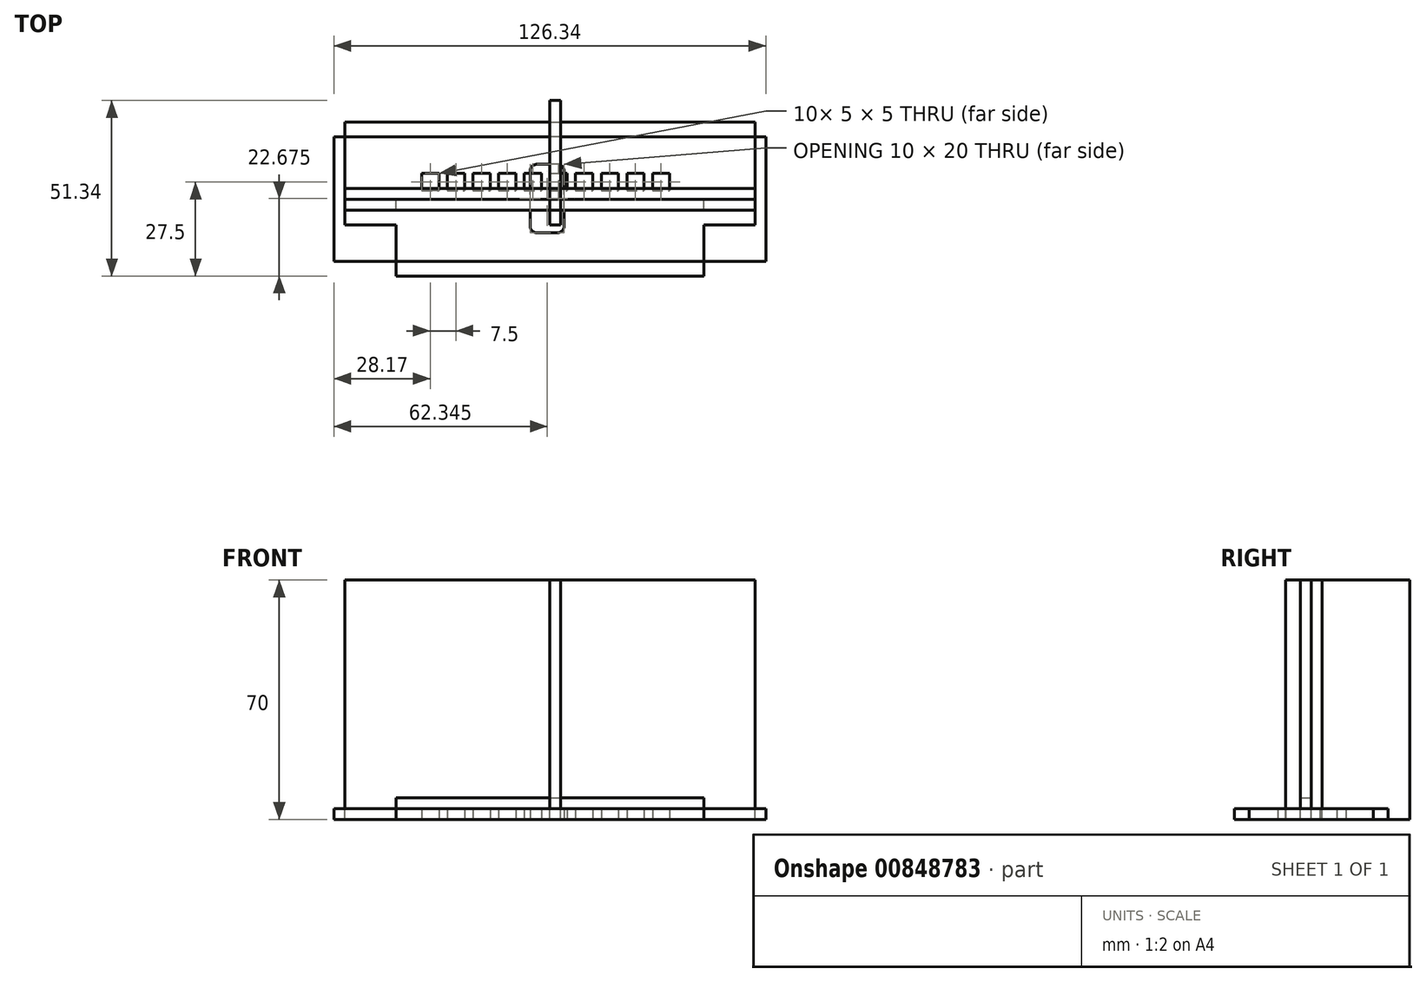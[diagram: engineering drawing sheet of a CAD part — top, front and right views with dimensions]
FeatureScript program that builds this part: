
annotation { "Feature Type Name" : "Feature", "Feature Type Description" : "" }
export const myFeature = defineFeature(function(context is Context, id is Id, definition is map)
    precondition{}
    {
        {
            var Q0;
            Q0=qCreatedBy(makeId("Top.planeOp"),FACE);
            var sketch = newSketch(context, id + "F0", { "sketchPlane" : qUnion([Q0])});
            skLineSegment(sketch, "E0.bottom", {"start": v(45, -22.5) * mm, "end": v(-45, -22.5) * mm});
            skLineSegment(sketch, "E0.top", {"start": v(45, 22.5) * mm, "end": v(-45, 22.5) * mm});
            skLineSegment(sketch, "E0.left", {"start": v(45, -22.5) * mm, "end": v(45, 22.5) * mm});
            skLineSegment(sketch, "E0.right", {"start": v(-45, -22.5) * mm, "end": v(-45, 22.5) * mm});
            skPoint(sketch, "E0.middle", {"position": v(0, 0) * mm});
            skLineSegment(sketch, "E1.bottom", {"start": v(-45, 22.5) * mm, "end": v(-60, 22.5) * mm});
            skLineSegment(sketch, "E1.left", {"start": v(-45, 22.5) * mm, "end": v(-45, -22.5) * mm});
            skLineSegment(sketch, "E2.bottom", {"start": v(-60, -7.5) * mm, "end": v(-45, -7.5) * mm});
            skLineSegment(sketch, "E2.right", {"start": v(-45, -7.5) * mm, "end": v(-45, -10.68) * mm});
            skLineSegment(sketch, "E3.MirrorCS", {"start": v(45, 22.5) * mm, "end": v(60, 22.5) * mm});
            skLineSegment(sketch, "E4.MirrorCS", {"start": v(60, -7.5) * mm, "end": v(45, -7.5) * mm});
            skLineSegment(sketch, "E5.bottom", {"start": v(-37.5, 7.5) * mm, "end": v(-32.5, 7.5) * mm});
            skLineSegment(sketch, "E5.top", {"start": v(-37.5, 2.5) * mm, "end": v(-32.5, 2.5) * mm});
            skLineSegment(sketch, "E5.left", {"start": v(-37.5, 7.5) * mm, "end": v(-37.5, 2.5) * mm});
            skLineSegment(sketch, "E5.right", {"start": v(-32.5, 7.5) * mm, "end": v(-32.5, 2.5) * mm});
            skLineSegment(sketch, "E6.1.0.0", {"start": v(-30, 7.5) * mm, "end": v(-25, 7.5) * mm});
            skLineSegment(sketch, "E6.1.0.1", {"start": v(-30, 7.5) * mm, "end": v(-30, 2.5) * mm});
            skLineSegment(sketch, "E6.1.0.2", {"start": v(-30, 2.5) * mm, "end": v(-25, 2.5) * mm});
            skLineSegment(sketch, "E6.1.0.3", {"start": v(-25, 7.5) * mm, "end": v(-25, 2.5) * mm});
            skLineSegment(sketch, "E6.2.0.0", {"start": v(-22.5, 7.5) * mm, "end": v(-17.5, 7.5) * mm});
            skLineSegment(sketch, "E6.2.0.1", {"start": v(-22.5, 7.5) * mm, "end": v(-22.5, 2.5) * mm});
            skLineSegment(sketch, "E6.2.0.2", {"start": v(-22.5, 2.5) * mm, "end": v(-17.5, 2.5) * mm});
            skLineSegment(sketch, "E6.2.0.3", {"start": v(-17.5, 7.5) * mm, "end": v(-17.5, 2.5) * mm});
            skLineSegment(sketch, "E6.3.0.0", {"start": v(-15, 7.5) * mm, "end": v(-10, 7.5) * mm});
            skLineSegment(sketch, "E6.3.0.1", {"start": v(-15, 7.5) * mm, "end": v(-15, 2.5) * mm});
            skLineSegment(sketch, "E6.3.0.2", {"start": v(-15, 2.5) * mm, "end": v(-10, 2.5) * mm});
            skLineSegment(sketch, "E6.3.0.3", {"start": v(-10, 7.5) * mm, "end": v(-10, 2.5) * mm});
            skLineSegment(sketch, "E6.4.0.0", {"start": v(-7.5, 7.5) * mm, "end": v(-2.5, 7.5) * mm});
            skLineSegment(sketch, "E6.4.0.1", {"start": v(-7.5, 7.5) * mm, "end": v(-7.5, 2.5) * mm});
            skLineSegment(sketch, "E6.4.0.2", {"start": v(-7.5, 2.5) * mm, "end": v(-2.5, 2.5) * mm});
            skLineSegment(sketch, "E6.4.0.3", {"start": v(-2.5, 7.5) * mm, "end": v(-2.5, 2.5) * mm});
            skLineSegment(sketch, "E6.5.0.0", {"start": v(0, 7.5) * mm, "end": v(5, 7.5) * mm});
            skLineSegment(sketch, "E6.5.0.1", {"start": v(0, 7.5) * mm, "end": v(0, 2.5) * mm});
            skLineSegment(sketch, "E6.5.0.2", {"start": v(0, 2.5) * mm, "end": v(5, 2.5) * mm});
            skLineSegment(sketch, "E6.5.0.3", {"start": v(5, 7.5) * mm, "end": v(5, 2.5) * mm});
            skLineSegment(sketch, "E6.6.0.0", {"start": v(7.5, 7.5) * mm, "end": v(12.5, 7.5) * mm});
            skLineSegment(sketch, "E6.6.0.1", {"start": v(7.5, 7.5) * mm, "end": v(7.5, 2.5) * mm});
            skLineSegment(sketch, "E6.6.0.2", {"start": v(7.5, 2.5) * mm, "end": v(12.5, 2.5) * mm});
            skLineSegment(sketch, "E6.6.0.3", {"start": v(12.5, 7.5) * mm, "end": v(12.5, 2.5) * mm});
            skLineSegment(sketch, "E6.7.0.0", {"start": v(15, 7.5) * mm, "end": v(20, 7.5) * mm});
            skLineSegment(sketch, "E6.7.0.1", {"start": v(15, 7.5) * mm, "end": v(15, 2.5) * mm});
            skLineSegment(sketch, "E6.7.0.2", {"start": v(15, 2.5) * mm, "end": v(20, 2.5) * mm});
            skLineSegment(sketch, "E6.7.0.3", {"start": v(20, 7.5) * mm, "end": v(20, 2.5) * mm});
            skLineSegment(sketch, "E6.8.0.0", {"start": v(22.5, 7.5) * mm, "end": v(27.5, 7.5) * mm});
            skLineSegment(sketch, "E6.8.0.1", {"start": v(22.5, 7.5) * mm, "end": v(22.5, 2.5) * mm});
            skLineSegment(sketch, "E6.8.0.2", {"start": v(22.5, 2.5) * mm, "end": v(27.5, 2.5) * mm});
            skLineSegment(sketch, "E6.8.0.3", {"start": v(27.5, 7.5) * mm, "end": v(27.5, 2.5) * mm});
            skLineSegment(sketch, "E6.9.0.0", {"start": v(30, 7.5) * mm, "end": v(35, 7.5) * mm});
            skLineSegment(sketch, "E6.9.0.1", {"start": v(30, 7.5) * mm, "end": v(30, 2.5) * mm});
            skLineSegment(sketch, "E6.9.0.2", {"start": v(30, 2.5) * mm, "end": v(35, 2.5) * mm});
            skLineSegment(sketch, "E6.9.0.3", {"start": v(35, 7.5) * mm, "end": v(35, 2.5) * mm});
            skLineSegment(sketch, "E6.direction1", {"start": v(-37.5, 7.5) * mm, "end": v(-30, 7.5) * mm, "construction": true});
            skPoint(sketch, "E7.middle", {"position": v(0, 18.18) * mm});
            skLineSegment(sketch, "E8", {"start": v(-60, -7.5) * mm, "end": v(-60, 22.5) * mm});
            skLineSegment(sketch, "E9", {"start": v(60, 22.5) * mm, "end": v(60, -7.5) * mm});
            skSolve(sketch);
        }
        {
            var Q0;
            {var subQ0=sQuery(id+"F0.wireOp",EDGE,"1d0d9cd3-5991-4caf-813b-380c669309750.MirrorCS");Q0=makeQuery(id+"F0.imprint","IMPRINT",FACE,{"disambiguationData":[TD([[makeQuery(id+"F0.imprint","IMPRINT",EDGE,{"derivedFrom":subQ0}),1.0]])]});}
            var Q1;
            {var subQ0=sQuery(id+"F0.wireOp",EDGE,"E3.MirrorCS");Q1=makeQuery(id+"F0.imprint","IMPRINT",FACE,{"disambiguationData":[TD([[makeQuery(id+"F0.imprint","IMPRINT",EDGE,{"derivedFrom":subQ0}),-1.0]])]});}
            var Q2;
            {var subQ0=sQuery(id+"F0.wireOp",EDGE,"E1.bottom");Q2=makeQuery(id+"F0.imprint","IMPRINT",FACE,{"disambiguationData":[TD([[makeQuery(id+"F0.imprint","IMPRINT",EDGE,{"derivedFrom":subQ0}),1.0]])]});}
            var Q3;
            {var subQ0=sQuery(id+"F0.wireOp",EDGE,"E1.top");Q3=makeQuery(id+"F0.imprint","IMPRINT",FACE,{"disambiguationData":[TD([[makeQuery(id+"F0.imprint","IMPRINT",EDGE,{"derivedFrom":subQ0}),-1.0]])]});}
            var Q4;
            {var subQ4=sQuery(id+"F0.wireOp",EDGE,"E0.bottom");Q4=makeQuery(id+"F0.imprint","IMPRINT",FACE,{"disambiguationData":[TD([[makeQuery(id+"F0.imprint","IMPRINT",EDGE,{"derivedFrom":subQ4}),-1.0]])]});}
            var Q5;
            Q5=makeQuery(id+"F0.imprint","IMPRINT",FACE,{"disambiguationData":[TD([[makeQuery(id+"F0.imprint","IMPRINT",EDGE,{"derivedFrom":sQuery(id+"F0.wireOp",EDGE,"E5.bottom")}),1.0]])]});
            var Q6;
            {var subQ5=sQuery(id+"F0.wireOp",EDGE,"E7.bottom");Q6=makeQuery(id+"F0.imprint","IMPRINT",FACE,{"disambiguationData":[TD([[makeQuery(id+"F0.imprint","IMPRINT",EDGE,{"derivedFrom":subQ5}),-1.0]])]});}
            var Q7;
            {var subQ0=sQuery(id+"F0.wireOp",EDGE,"E2.bottom");Q7=makeQuery(id+"F0.imprint","IMPRINT",FACE,{"disambiguationData":[TD([[makeQuery(id+"F0.imprint","IMPRINT",EDGE,{"derivedFrom":subQ0}),1.0]])]});}
            var Q8;
            {var subQ0=sQuery(id+"F0.wireOp",EDGE,"E4.MirrorCS");Q8=makeQuery(id+"F0.imprint","IMPRINT",FACE,{"disambiguationData":[TD([[makeQuery(id+"F0.imprint","IMPRINT",EDGE,{"derivedFrom":subQ0}),-1.0]])]});}
            extrude(context, id + "F1", {"entities" : qUnion([Q0, Q1, Q2, Q3, Q4, Q5, Q6, Q7, Q8]), "depth" : 3.17 * mm, "offsetDistance" : 25 * mm});
        }
        {
            var Q0;
            Q0=qCreatedBy(makeId("Front.planeOp"),FACE);
            var sketch = newSketch(context, id + "F2", { "sketchPlane" : qUnion([Q0])});
            skLineSegment(sketch, "E10.bottom", {"start": v(-60, 0) * mm, "end": v(60, 0) * mm});
            skLineSegment(sketch, "E10.top", {"start": v(-60, 70) * mm, "end": v(60, 70) * mm});
            skLineSegment(sketch, "E10.left", {"start": v(-60, 0) * mm, "end": v(-60, 70) * mm});
            skLineSegment(sketch, "E10.right", {"start": v(60, 0) * mm, "end": v(60, 70) * mm});
            skLineSegment(sketch, "E11.bottom", {"start": v(-45, 0) * mm, "end": v(45, 0) * mm});
            skLineSegment(sketch, "E11.top", {"start": v(-45, 6.35) * mm, "end": v(45, 6.35) * mm});
            skLineSegment(sketch, "E11.left", {"start": v(-45, 0) * mm, "end": v(-45, 6.35) * mm});
            skLineSegment(sketch, "E11.right", {"start": v(45, 0) * mm, "end": v(45, 6.35) * mm});
            skSolve(sketch);
        }
        {
            var Q0;
            Q0=makeQuery(id+"F2.imprint","IMPRINT",FACE,{"disambiguationData":[TD([[makeQuery(id+"F2.imprint","IMPRINT",EDGE,{"derivedFrom":sQuery(id+"F2.wireOp",EDGE,"E10.top")}),-1.0]])]});
            extrude(context, id + "F3", {"entities" : qUnion([Q0]), "depth" : 3.17 * mm, "offsetDistance" : 25 * mm});
        }
        {
            var Q0;
            Q0 = qSketchRegion(id + "F2", true);
            extrude(context, id + "F4", {"entities" : qUnion([Q0]), "oppositeDirection" : true, "depth" : 3.17 * mm, "offsetDistance" : 25 * mm});
        }
        {
            var Q0;
            Q0=qCreatedBy(makeId("Right.planeOp"),FACE);
            var sketch = newSketch(context, id + "F5", { "sketchPlane" : qUnion([Q0])});
            skLineSegment(sketch, "E12.bottom", {"start": v(-7.51, 0) * mm, "end": v(28.84, 0) * mm});
            skLineSegment(sketch, "E12.top", {"start": v(-7.51, 70) * mm, "end": v(28.84, 70) * mm});
            skLineSegment(sketch, "E12.left", {"start": v(-7.51, 0) * mm, "end": v(-7.51, 70) * mm});
            skLineSegment(sketch, "E12.right", {"start": v(28.84, 0) * mm, "end": v(28.84, 70) * mm});
            skSolve(sketch);
        }
        {
            var Q0;
            Q0=makeQuery(id+"F5.imprint","IMPRINT",FACE,{"disambiguationData":[TD([[makeQuery(id+"F5.imprint","IMPRINT",EDGE,{"derivedFrom":sQuery(id+"F5.wireOp",EDGE,"E12.bottom")}),1.0]])]});
            extrude(context, id + "F6", {"entities" : qUnion([Q0]), "depth" : 3.17 * mm, "offsetDistance" : 25 * mm});
        }
        {
            var Q0;
            Q0=qCreatedBy(makeId("Top.planeOp"),FACE);
            var sketch = newSketch(context, id + "F7", { "sketchPlane" : qUnion([Q0])});
            skLineSegment(sketch, "E13.bottom", {"start": v(63.17, -18.17) * mm, "end": v(-63.17, -18.18) * mm});
            skLineSegment(sketch, "E13.top", {"start": v(63.17, 18.18) * mm, "end": v(-63.17, 18.17) * mm});
            skLineSegment(sketch, "E13.left", {"start": v(63.17, -18.17) * mm, "end": v(63.17, 18.18) * mm});
            skLineSegment(sketch, "E13.right", {"start": v(-63.17, -18.18) * mm, "end": v(-63.17, 18.17) * mm});
            skPoint(sketch, "E13.middle", {"position": v(0, 0) * mm});
            skLineSegment(sketch, "E14.bottom", {"start": v(4.17, -9.83) * mm, "end": v(-5.83, -9.83) * mm});
            skLineSegment(sketch, "E14.top", {"start": v(4.17, 10.17) * mm, "end": v(-5.83, 10.17) * mm});
            skLineSegment(sketch, "E14.left", {"start": v(4.17, -9.83) * mm, "end": v(4.17, 10.17) * mm});
            skLineSegment(sketch, "E14.right", {"start": v(-5.83, -9.83) * mm, "end": v(-5.83, 10.17) * mm});
            skPoint(sketch, "E14.middle", {"position": v(-0.83, 0.17) * mm});
            skSolve(sketch);
        }
        {
            var Q0;
            Q0 = qSketchRegion(id + "F7", true);
            extrude(context, id + "F8", {"entities" : qUnion([Q0]), "depth" : 3.17 * mm, "offsetDistance" : 25 * mm});
        }
        {
            var Q0;
            Q0=makeQuery(id+"F8.opExtrude","SWEPT_EDGE",EDGE,{"disambiguationData":[OSD([sQuery(id+"F7.wireOp",EDGE,"E14.top"),sQuery(id+"F7.wireOp",EDGE,"E14.right")])]});
            var Q1;
            Q1=makeQuery(id+"F8.opExtrude","SWEPT_EDGE",EDGE,{"disambiguationData":[OSD([sQuery(id+"F7.wireOp",EDGE,"E14.top"),sQuery(id+"F7.wireOp",EDGE,"E14.left")])]});
            var Q2;
            Q2=makeQuery(id+"F8.opExtrude","SWEPT_EDGE",EDGE,{"disambiguationData":[OSD([sQuery(id+"F7.wireOp",EDGE,"E14.bottom"),sQuery(id+"F7.wireOp",EDGE,"E14.left")])]});
            var Q3;
            Q3=makeQuery(id+"F8.opExtrude","SWEPT_EDGE",EDGE,{"disambiguationData":[OSD([sQuery(id+"F7.wireOp",EDGE,"E14.bottom"),sQuery(id+"F7.wireOp",EDGE,"E14.right")])]});
            fillet(context, id + "F9", {"entities" : qUnion([Q0, Q1, Q2, Q3]), "radius" : 2 * mm, "tangentPropagation" : true, "allowEdgeOverflow" : false});
        }
    });
